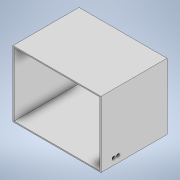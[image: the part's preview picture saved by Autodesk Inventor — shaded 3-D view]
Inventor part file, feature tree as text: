
AUTODESK INVENTOR PART (.ipt)
format: ipt  version: 2020 (Build 240168000, 168)  size: 126,464 bytes
history: native  units: mm
features: extrude x3, sketch x3, shell x1
ambient origin geometry x8: Origin, YZ Plane, XZ Plane, XY Plane, X Axis, Y Axis, Z Axis, Center Point
bodies: Solid1 (feature_tree)
feature tree (7):
  extrude  "Base"  Depth=300.0mm
  shell  "Shell1"  Thickness=300.0mm
  extrude  "40 mm fan mout holes"  Depth=5.0mm
  extrude  "Cable Holes"  Depth=10.0mm
  sketch  "Sketch2"  dims[d0=400.0mm d1=300.0mm d2=300.0mm d3=0.0mm]
  sketch  "Sketch3"  dims[d4=5.0mm d5=4.3mm]
  sketch  "Sketch4"  dims[d6=20.0mm d8=32.0mm d9=20.0mm d11=32.0mm d14=32.15mm d15=32.15mm d16=300.0mm d17=0.0mm d18=15.0mm d19=57.5mm d20=28.75mm d21=20.0mm d23=20.0mm d24=10.0mm d26=10.0mm d28=10.0mm d29=0.0mm]
